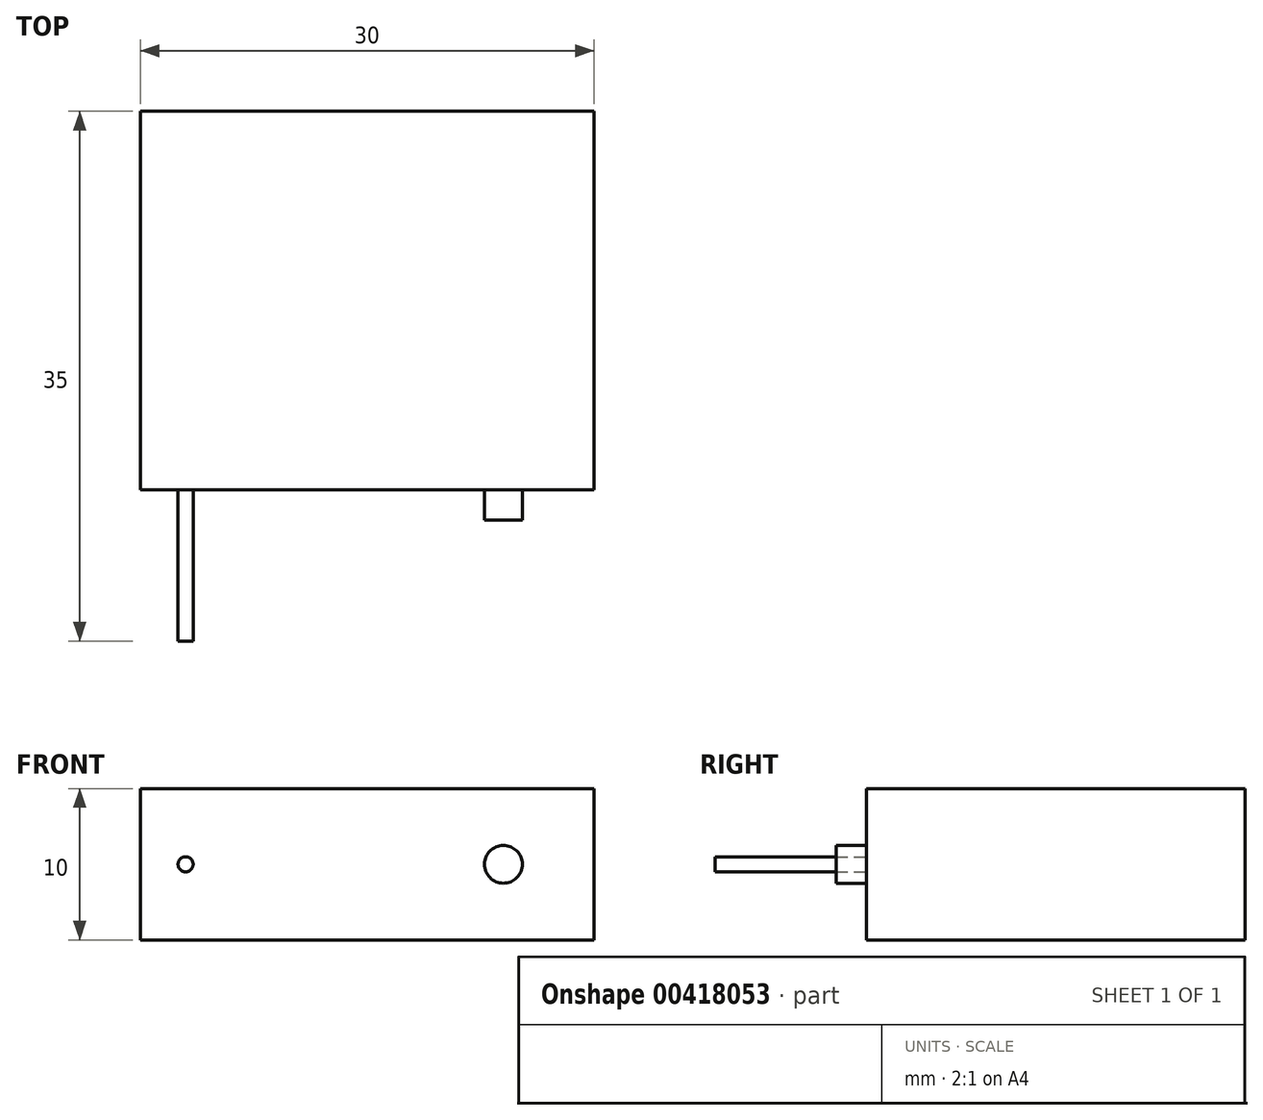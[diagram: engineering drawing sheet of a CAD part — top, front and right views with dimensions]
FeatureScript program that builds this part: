
annotation { "Feature Type Name" : "Feature", "Feature Type Description" : "" }
export const myFeature = defineFeature(function(context is Context, id is Id, definition is map)
    precondition{}
    {
        {
            var Q0;
            Q0=qCreatedBy(makeId("Front.planeOp"),FACE);
            var sketch = newSketch(context, id + "F0", { "sketchPlane" : qUnion([Q0])});
            skLineSegment(sketch, "E0.bottom", {"start": v(-46, 10) * mm, "end": v(-16, 10) * mm});
            skLineSegment(sketch, "E0.top", {"start": v(-46, 0) * mm, "end": v(-16, 0) * mm});
            skLineSegment(sketch, "E0.left", {"start": v(-46, 10) * mm, "end": v(-46, 0) * mm});
            skLineSegment(sketch, "E0.right", {"start": v(-16, 10) * mm, "end": v(-16, 0) * mm});
            skSolve(sketch);
        }
        {
            var Q0;
            Q0=qSketchRegion(id+"F0",true);
            extrude(context, id + "F1", {"entities" : qUnion([Q0]), "depth" : -25 * mm});
        }
        {
            var Q0;
            Q0=makeQuery(id+"F1.opExtrude","CAP_FACE",FACE,{"disambiguationData":[OSD([sQuery(id+"F0.wireOp",EDGE,"E0.bottom"),sQuery(id+"F0.wireOp",EDGE,"E0.top"),sQuery(id+"F0.wireOp",EDGE,"E0.left"),sQuery(id+"F0.wireOp",EDGE,"E0.right")])],"isStart":true});
            var sketch = newSketch(context, id + "F2", { "sketchPlane" : qUnion([Q0])});
            skCircle(sketch, "E1", {"center": v(-22, 5) * mm, "radius": 1.25 * mm});
            skSolve(sketch);
        }
        {
            var Q0;
            Q0=qSketchRegion(id+"F2",true);
            extrude(context, id + "F3", {"entities" : qUnion([Q0]), "operationType" : NewBodyOperationType.ADD, "depth" : 2 * mm});
        }
        {
            var Q0;
            Q0=makeQuery(id+"F1.opExtrude","CAP_FACE",FACE,{"disambiguationData":[OSD([sQuery(id+"F0.wireOp",EDGE,"E0.bottom"),sQuery(id+"F0.wireOp",EDGE,"E0.top"),sQuery(id+"F0.wireOp",EDGE,"E0.left"),sQuery(id+"F0.wireOp",EDGE,"E0.right")])],"isStart":true});
            var sketch = newSketch(context, id + "F4", { "sketchPlane" : qUnion([Q0])});
            skCircle(sketch, "E2", {"center": v(-43, 5) * mm, "radius": 0.5 * mm});
            skSolve(sketch);
        }
        {
            var Q0;
            Q0=qSketchRegion(id+"F4",true);
            extrude(context, id + "F5", {"entities" : qUnion([Q0]), "operationType" : NewBodyOperationType.ADD, "depth" : 10 * mm});
        }
    });
